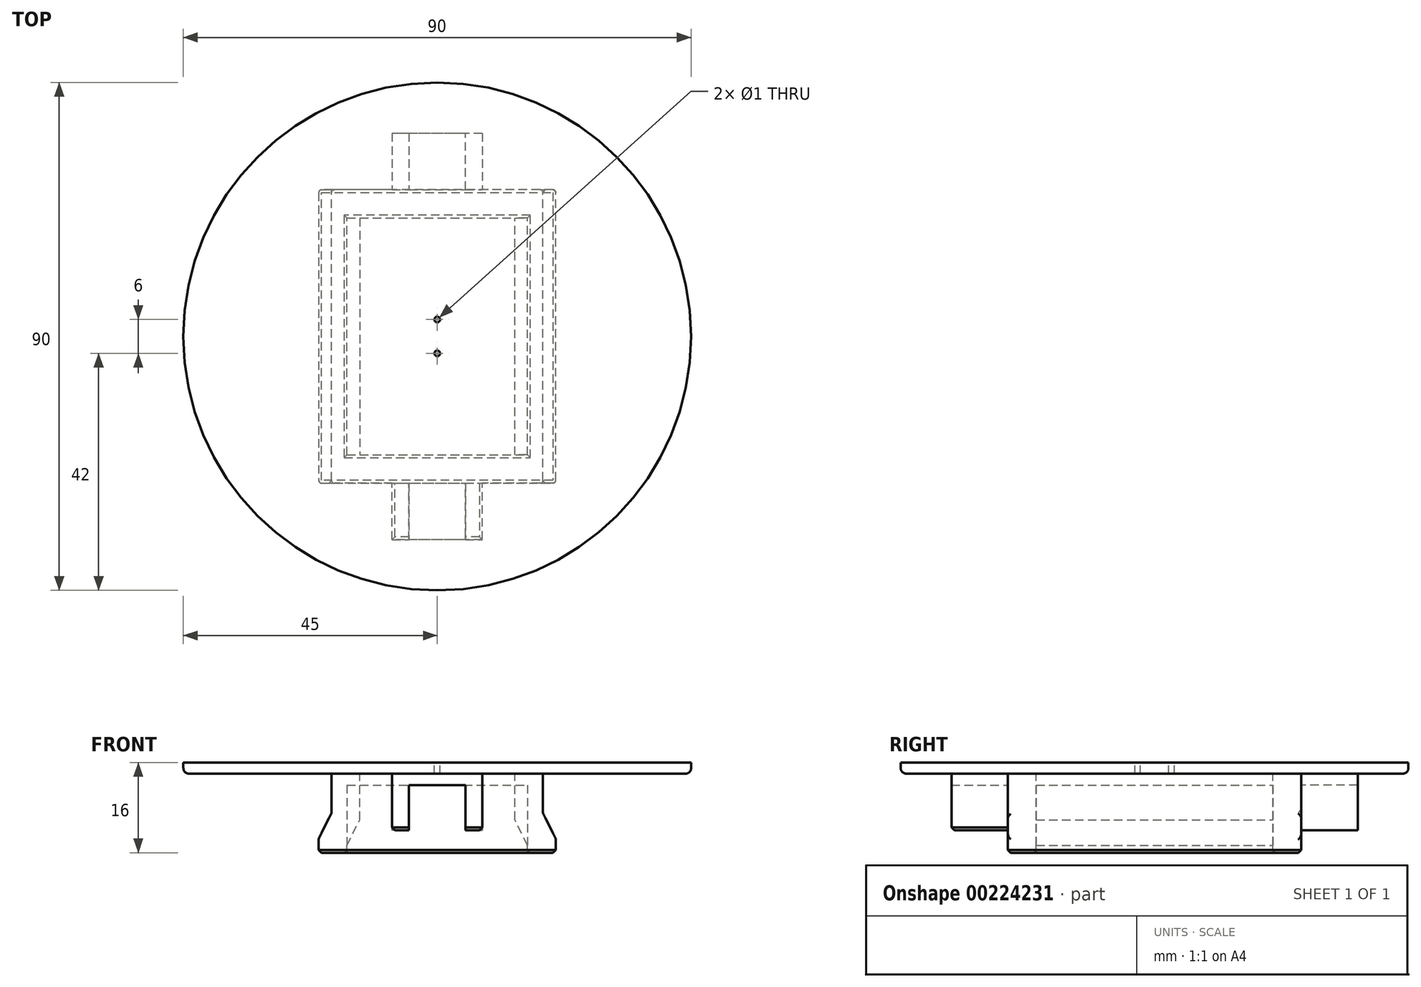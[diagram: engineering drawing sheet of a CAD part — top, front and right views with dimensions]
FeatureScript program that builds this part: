
annotation { "Feature Type Name" : "Feature", "Feature Type Description" : "" }
export const myFeature = defineFeature(function(context is Context, id is Id, definition is map)
    precondition{}
    {
        {
            var Q0;
            Q0=qCreatedBy(makeId("Top.planeOp"),FACE);
            var sketch = newSketch(context, id + "F0", { "sketchPlane" : qUnion([Q0])});
            skCircle(sketch, "E0", {"center": v(0, 0) * mm, "radius": 45 * mm});
            skSolve(sketch);
        }
        {
            var Q0;
            Q0 = qSketchRegion(id + "F0", true);
            extrude(context, id + "F1", {"entities" : qUnion([Q0]), "depth" : 2 * mm});
        }
        {
            var Q0;
            Q0=qCreatedBy(makeId("Front.planeOp"),FACE);
            var sketch = newSketch(context, id + "F2", { "sketchPlane" : qUnion([Q0])});
            skPoint(sketch, "E1.MirrorCS.end.orphan", {"position": v(0, -14) * mm});
            skPoint(sketch, "E2.MirrorCS.start.orphan", {"position": v(0, 0) * mm});
            skLineSegment(sketch, "E3", {"start": v(-18.75, -7) * mm, "end": v(-18.75, -14) * mm, "construction": true});
            skLineSegment(sketch, "E4", {"start": v(-18.75, -7) * mm, "end": v(-18.75, 0) * mm});
            skLineSegment(sketch, "E5", {"start": v(-21, -14) * mm, "end": v(-21, -11.5) * mm});
            skLineSegment(sketch, "E6", {"start": v(-21, -11.5) * mm, "end": v(-18.75, -7) * mm});
            skLineSegment(sketch, "E7", {"start": v(-18.75, 0) * mm, "end": v(0, 0) * mm});
            skLineSegment(sketch, "E8", {"start": v(-21, -14) * mm, "end": v(0, -14) * mm});
            skLineSegment(sketch, "E9", {"start": v(0, 0) * mm, "end": v(0, -14) * mm, "construction": true});
            skLineSegment(sketch, "E10.MirrorCS", {"start": v(21, -14) * mm, "end": v(21, -11.5) * mm});
            skLineSegment(sketch, "E11.MirrorCS", {"start": v(18.75, 0) * mm, "end": v(0, 0) * mm});
            skLineSegment(sketch, "E12.MirrorCS", {"start": v(21, -14) * mm, "end": v(0, -14) * mm});
            skLineSegment(sketch, "E13.MirrorCS", {"start": v(18.75, -7) * mm, "end": v(18.75, -14) * mm, "construction": true});
            skLineSegment(sketch, "E14.MirrorCS", {"start": v(18.75, -7) * mm, "end": v(18.75, 0) * mm});
            skLineSegment(sketch, "E15.MirrorCS", {"start": v(21, -11.5) * mm, "end": v(18.75, -7) * mm});
            skSolve(sketch);
        }
        {
            var Q0;
            Q0=makeQuery(id+"F2.imprint","IMPRINT",FACE,{"disambiguationData":[TD([[makeQuery(id+"F2.imprint","IMPRINT",EDGE,{"derivedFrom":sQuery(id+"F2.wireOp",EDGE,"E4")}),-1.0]])]});
            extrude(context, id + "F3", {"entities" : qUnion([Q0]), "operationType" : NewBodyOperationType.ADD, "depth" : 26 * mm, "hasSecondDirection" : true, "secondDirectionOppositeDirection" : true, "secondDirectionDepth" : 26 * mm});
        }
        {
            var Q0;
            Q0=makeQuery(id+"F3.opExtrude","SWEPT_FACE",FACE,{"disambiguationData":[OSD([sQuery(id+"F2.wireOp",EDGE,"E8"),sQuery(id+"F2.wireOp",EDGE,"E12.MirrorCS")])]});
            shell(context, id + "F4", {"entities" : qUnion([Q0]), "thickness" : 5 * mm});
        }
        {
            var Q0;
            Q0=makeQuery(id+"F1.opExtrude","CAP_FACE",FACE,{"disambiguationData":[OSD([sQuery(id+"F0.wireOp",EDGE,"E0")])],"isStart":false});
            var sketch = newSketch(context, id + "F5", { "sketchPlane" : qUnion([Q0])});
            skLineSegment(sketch, "E16", {"start": v(0, 3) * mm, "end": v(0, -3) * mm, "construction": true});
            skSolve(sketch);
        }
        {
            var Q0;
            Q0=sQuery(id+"F5.wireOp",VERTEX,"E16.end");
            var Q1;
            Q1=sQuery(id+"F5.wireOp",VERTEX,"E16.start");
            var Q2;
            Q2=makeQuery(id+"F1.opExtrude","SWEPT_BODY",BODY,{"disambiguationData":[OSD([sQuery(id+"F0.wireOp",EDGE,"E0")])]});
            hole(context, id + "F6", {"style" : HoleStyle.SIMPLE, "endStyle" : HoleEndStyle.THROUGH, "holeDiameter" : 1 * mm, "tappedDepth" : 12 * mm, "tapClearance" : 3, "locations" : qUnion([Q0, Q1]), "scope" : qUnion([Q2])});
        }
        {
            var Q0;
            Q0=makeQuery(id+"F1.opExtrude","CAP_EDGE",EDGE,{"disambiguationData":[OSD([sQuery(id+"F0.wireOp",EDGE,"E0")])],"isStart":true});
            fillet(context, id + "F7", {"entities" : qUnion([Q0]), "radius" : 1 * mm, "tangentPropagation" : true, "allowEdgeOverflow" : false});
        }
        {
            var Q0;
            Q0=makeQuery(id+"F3.opExtrude","SWEPT_EDGE",EDGE,{"disambiguationData":[OSD([sQuery(id+"F2.wireOp",EDGE,"E5"),sQuery(id+"F2.wireOp",EDGE,"E6")])]});
            var Q1;
            Q1=makeQuery(id+"F3.opExtrude","SWEPT_EDGE",EDGE,{"disambiguationData":[OSD([sQuery(id+"F2.wireOp",EDGE,"E4"),sQuery(id+"F2.wireOp",EDGE,"E6")])]});
            var Q2;
            Q2=makeQuery(id+"F3.opExtrude","CAP_EDGE",EDGE,{"disambiguationData":[OSD([sQuery(id+"F2.wireOp",EDGE,"E4")])],"isStart":false});
            var Q3;
            Q3=makeQuery(id+"F3.opExtrude","CAP_EDGE",EDGE,{"disambiguationData":[OSD([sQuery(id+"F2.wireOp",EDGE,"E5")])],"isStart":false});
            var Q4;
            Q4=makeQuery(id+"F3.opExtrude","CAP_EDGE",EDGE,{"disambiguationData":[OSD([sQuery(id+"F2.wireOp",EDGE,"E5")])],"isStart":true});
            var Q5;
            Q5=makeQuery(id+"F3.opExtrude","CAP_EDGE",EDGE,{"disambiguationData":[OSD([sQuery(id+"F2.wireOp",EDGE,"E6")])],"isStart":true});
            var Q6;
            Q6=makeQuery(id+"F3.opExtrude","SWEPT_EDGE",EDGE,{"disambiguationData":[OSD([sQuery(id+"F2.wireOp",EDGE,"E14.MirrorCS"),sQuery(id+"F2.wireOp",EDGE,"E15.MirrorCS")])]});
            var Q7;
            Q7=makeQuery(id+"F3.opExtrude","SWEPT_EDGE",EDGE,{"disambiguationData":[OSD([sQuery(id+"F2.wireOp",EDGE,"E10.MirrorCS"),sQuery(id+"F2.wireOp",EDGE,"E15.MirrorCS")])]});
            var Q8;
            Q8=makeQuery(id+"F3.opExtrude","CAP_EDGE",EDGE,{"disambiguationData":[OSD([sQuery(id+"F2.wireOp",EDGE,"E14.MirrorCS")])],"isStart":true});
            var Q9;
            Q9=makeQuery(id+"F3.opExtrude","CAP_EDGE",EDGE,{"disambiguationData":[OSD([sQuery(id+"F2.wireOp",EDGE,"E10.MirrorCS")])],"isStart":true});
            var Q10;
            Q10=makeQuery(id+"F3.opExtrude","CAP_EDGE",EDGE,{"disambiguationData":[OSD([sQuery(id+"F2.wireOp",EDGE,"E10.MirrorCS")])],"isStart":false});
            var Q11;
            Q11=makeQuery(id+"F3.opExtrude","CAP_EDGE",EDGE,{"disambiguationData":[OSD([sQuery(id+"F2.wireOp",EDGE,"E14.MirrorCS")])],"isStart":false});
            fillet(context, id + "F8", {"entities" : qUnion([Q0, Q1, Q2, Q3, Q4, Q5, Q6, Q7, Q8, Q9, Q10, Q11]), "radius" : .5 * mm, "tangentPropagation" : true, "allowEdgeOverflow" : false});
        }
        {
            var Q0;
            Q0=makeQuery(id+"F4.opShell","OFFSET_FACE",FACE,{"disambiguationData":[OSD([sQuery(id+"F0.wireOp",EDGE,"E0")])]});
            extrude(context, id + "F9", {"entities" : qUnion([Q0]), "operationType" : NewBodyOperationType.REMOVE, "oppositeDirection" : true, "depth" : 3 * mm});
        }
        {
            var Q0;
            Q0=makeQuery(id+"F3.opExtrude","CAP_FACE",FACE,{"disambiguationData":[OSD([sQuery(id+"F2.wireOp",EDGE,"E4"),sQuery(id+"F2.wireOp",EDGE,"E5"),sQuery(id+"F2.wireOp",EDGE,"E6"),sQuery(id+"F2.wireOp",EDGE,"E7"),sQuery(id+"F2.wireOp",EDGE,"E8"),sQuery(id+"F2.wireOp",EDGE,"E10.MirrorCS"),sQuery(id+"F2.wireOp",EDGE,"E11.MirrorCS"),sQuery(id+"F2.wireOp",EDGE,"E12.MirrorCS"),sQuery(id+"F2.wireOp",EDGE,"E14.MirrorCS"),sQuery(id+"F2.wireOp",EDGE,"E15.MirrorCS")])],"isStart":false});
            var sketch = newSketch(context, id + "F10", { "sketchPlane" : qUnion([Q0])});
            skLineSegment(sketch, "E17", {"start": v(0, 0) * mm, "end": v(8, 0) * mm});
            skLineSegment(sketch, "E18", {"start": v(8, 0) * mm, "end": v(8, -10) * mm});
            skLineSegment(sketch, "E19", {"start": v(8, -10) * mm, "end": v(-8, -10) * mm});
            skLineSegment(sketch, "E20", {"start": v(-8, -10) * mm, "end": v(-8, 0) * mm});
            skLineSegment(sketch, "E21", {"start": v(-8, 0) * mm, "end": v(0, 0) * mm});
            skSolve(sketch);
        }
        {
            var Q0;
            Q0 = qSketchRegion(id + "F10", true);
            extrude(context, id + "F11", {"entities" : qUnion([Q0]), "depth" : 10 * mm, "offsetDistance" : 25 * mm, "hasSecondDirection" : true, "secondDirectionOppositeDirection" : true, "secondDirectionDepth" : 2 * mm});
        }
        {
            var Q0;
            Q0=makeQuery(id+"F11.opExtrude","SWEPT_BODY",BODY,{"disambiguationData":[OSD([sQuery(id+"F10.wireOp",EDGE,"E17"),sQuery(id+"F10.wireOp",EDGE,"E18"),sQuery(id+"F10.wireOp",EDGE,"E19"),sQuery(id+"F10.wireOp",EDGE,"E20"),sQuery(id+"F10.wireOp",EDGE,"E21")])]});
            var Q1;
            Q1=qCreatedBy(makeId("Front.planeOp"),FACE);
            mirror(context, id + "F12", {"operationType" : NewBodyOperationType.ADD, "entities" : qUnion([Q0]), "mirrorPlane" : qUnion([Q1])});
        }
        {
            var Q0;
            {var subQ0=makeQuery(id+"F11.opExtrude","SWEPT_FACE",FACE,{"disambiguationData":[OSD([sQuery(id+"F10.wireOp",EDGE,"E19")])]});Q0=makeQuery(id+"F12.boolean.opBoolean","MERGE",FACE,{"derivedFrom":[makeQuery(id+"F3.opExtrude","SWEPT_FACE",FACE,{"disambiguationData":[OSD([sQuery(id+"F2.wireOp",EDGE,"E8"),sQuery(id+"F2.wireOp",EDGE,"E12.MirrorCS")])]}),subQ0,makeQuery(id+"F12.opPattern","COPY",FACE,{"derivedFrom":subQ0,"instanceName":"1"})]});}
            var sketch = newSketch(context, id + "F13", { "sketchPlane" : qUnion([Q0])});
            skLineSegment(sketch, "E22", {"start": v(0, -36) * mm, "end": v(-5, -36) * mm});
            skLineSegment(sketch, "E23", {"start": v(-5, -36) * mm, "end": v(-5, -21) * mm});
            skLineSegment(sketch, "E24", {"start": v(-5, -21) * mm, "end": v(5, -21) * mm});
            skLineSegment(sketch, "E25", {"start": v(5, -21) * mm, "end": v(5, -36) * mm});
            skLineSegment(sketch, "E26", {"start": v(5, -36) * mm, "end": v(0, -36) * mm});
            skSolve(sketch);
        }
        {
            var Q0;
            Q0=makeQuery(id+"F13.imprint","IMPRINT",FACE,{"disambiguationData":[TD([[makeQuery(id+"F13.imprint","IMPRINT",EDGE,{"derivedFrom":sQuery(id+"F13.wireOp",EDGE,"E22")}),-1.0]])]});
            var Q1;
            {var subQ0=sQuery(id+"F13.wireOp",EDGE,"E24");Q1=makeQuery(id+"F13.imprint","IMPRINT",FACE,{"disambiguationData":[TD([[makeQuery(id+"F13.imprint","IMPRINT",EDGE,{"derivedFrom":subQ0}),1.0]])]});}
            extrude(context, id + "F14", {"entities" : qUnion([Q0, Q1]), "oppositeDirection" : true, "depth" : 12 * mm, "offsetDistance" : 25 * mm});
        }
        {
            var Q0;
            Q0=makeQuery(id+"F14.opExtrude","SWEPT_BODY",BODY,{"disambiguationData":[OSD([sQuery(id+"F13.wireOp",EDGE,"E22"),sQuery(id+"F13.wireOp",EDGE,"E23"),sQuery(id+"F13.wireOp",EDGE,"E24"),sQuery(id+"F13.wireOp",EDGE,"E25"),sQuery(id+"F13.wireOp",EDGE,"E26")])]});
            var Q1;
            Q1=qCreatedBy(makeId("Front.planeOp"),FACE);
            mirror(context, id + "F15", {"entities" : qUnion([Q0]), "mirrorPlane" : qUnion([Q1])});
        }
        {
            var Q0;
            Q0=makeQuery(id+"F14.opExtrude","SWEPT_BODY",BODY,{"disambiguationData":[OSD([sQuery(id+"F13.wireOp",EDGE,"E22"),sQuery(id+"F13.wireOp",EDGE,"E23"),sQuery(id+"F13.wireOp",EDGE,"E24"),sQuery(id+"F13.wireOp",EDGE,"E25"),sQuery(id+"F13.wireOp",EDGE,"E26")])]});
            var Q1;
            Q1=makeQuery(id+"F15.opPattern","COPY",BODY,{"derivedFrom":makeQuery(id+"F14.opExtrude","SWEPT_BODY",BODY,{"disambiguationData":[OSD([sQuery(id+"F13.wireOp",EDGE,"E22"),sQuery(id+"F13.wireOp",EDGE,"E23"),sQuery(id+"F13.wireOp",EDGE,"E24"),sQuery(id+"F13.wireOp",EDGE,"E25"),sQuery(id+"F13.wireOp",EDGE,"E26")])]}),"instanceName":"1"});
            var Q2;
            Q2=makeQuery(id+"F1.opExtrude","SWEPT_BODY",BODY,{"disambiguationData":[OSD([sQuery(id+"F0.wireOp",EDGE,"E0")])]});
            booleanBodies(context, id + "F16", {"operationType" : BooleanOperationType.SUBTRACTION, "tools" : qUnion([Q0, Q1]), "targets" : qUnion([Q2])});
        }
        {
            var Q0;
            {var subQ0=sQuery(id+"F2.wireOp",EDGE,"E12.MirrorCS");var subQ1=sQuery(id+"F2.wireOp",EDGE,"E10.MirrorCS");var subQ2=sQuery(id+"F2.wireOp",EDGE,"E8");var subQ4=makeQuery(id+"F3.opExtrude","CAP_EDGE",EDGE,{"disambiguationData":[OSD([subQ2,subQ0])],"isStart":false});Q0=makeQuery(id+"FFm1TcCdVZ59tot_1.boolean.opBoolean","SPLIT",EDGE,{"disambiguationData":[TD([makeQuery(id+"F3.opExtrude","SWEPT_FACE",FACE,{"disambiguationData":[OSD([subQ1])]})])],"derivedFrom":subQ4});}
            var Q1;
            {var subQ0=sQuery(id+"F2.wireOp",EDGE,"E12.MirrorCS");var subQ1=sQuery(id+"F2.wireOp",EDGE,"E8");var subQ2=sQuery(id+"F2.wireOp",EDGE,"E5");Q1=makeQuery(id+"FFm1TcCdVZ59tot_1.boolean.opBoolean","SPLIT",EDGE,{"disambiguationData":[TD([makeQuery(id+"F3.opExtrude","SWEPT_FACE",FACE,{"disambiguationData":[OSD([subQ2])]})])],"derivedFrom":makeQuery(id+"F3.opExtrude","CAP_EDGE",EDGE,{"disambiguationData":[OSD([subQ1,subQ0])],"isStart":true})});}
            var Q2;
            {var subQ0=sQuery(id+"F2.wireOp",EDGE,"E12.MirrorCS");var subQ1=sQuery(id+"F2.wireOp",EDGE,"E8");var subQ8=sQuery(id+"F2.wireOp",EDGE,"E5");var subQ11=makeQuery(id+"F3.opExtrude","CAP_EDGE",EDGE,{"disambiguationData":[OSD([subQ1,subQ0])],"isStart":false});Q2=makeQuery(id+"FFm1TcCdVZ59tot_1.boolean.opBoolean","SPLIT",EDGE,{"disambiguationData":[TD([makeQuery(id+"F4.opShell","OFFSET_FACE",FACE,{"disambiguationData":[OSD([subQ8])]})])],"derivedFrom":makeQuery(id+"F4.opShell","OFFSET_EDGE",EDGE,{"disambiguationData":[OSD([subQ1,subQ0]),TDD([subQ11])]})});}
            var Q3;
            {var subQ0=sQuery(id+"F2.wireOp",EDGE,"E12.MirrorCS");var subQ1=sQuery(id+"F2.wireOp",EDGE,"E8");var subQ5=sQuery(id+"F2.wireOp",EDGE,"E10.MirrorCS");Q3=makeQuery(id+"FFm1TcCdVZ59tot_1.boolean.opBoolean","SPLIT",EDGE,{"disambiguationData":[TD([makeQuery(id+"F4.opShell","OFFSET_FACE",FACE,{"disambiguationData":[OSD([subQ5])]})])],"derivedFrom":makeQuery(id+"F4.opShell","OFFSET_EDGE",EDGE,{"disambiguationData":[OSD([subQ1,subQ0]),TDD([makeQuery(id+"F3.opExtrude","CAP_EDGE",EDGE,{"disambiguationData":[OSD([subQ1,subQ0])],"isStart":true})])]})});}
            var Q4;
            Q4=makeQuery(id+"F4.opShell","OFFSET_EDGE",EDGE,{"disambiguationData":[OSD([sQuery(id+"F2.wireOp",EDGE,"E10.MirrorCS"),sQuery(id+"F2.wireOp",EDGE,"E12.MirrorCS")])]});
            var Q5;
            {var subQ0=sQuery(id+"F2.wireOp",EDGE,"E12.MirrorCS");var subQ1=sQuery(id+"F2.wireOp",EDGE,"E8");var subQ5=sQuery(id+"F2.wireOp",EDGE,"E10.MirrorCS");var subQ11=makeQuery(id+"F3.opExtrude","CAP_EDGE",EDGE,{"disambiguationData":[OSD([subQ1,subQ0])],"isStart":false});Q5=makeQuery(id+"FFm1TcCdVZ59tot_1.boolean.opBoolean","SPLIT",EDGE,{"disambiguationData":[TD([makeQuery(id+"F4.opShell","OFFSET_FACE",FACE,{"disambiguationData":[OSD([subQ5])]})])],"derivedFrom":makeQuery(id+"F4.opShell","OFFSET_EDGE",EDGE,{"disambiguationData":[OSD([subQ1,subQ0]),TDD([subQ11])]})});}
            var Q6;
            Q6=makeQuery(id+"F4.opShell","OFFSET_EDGE",EDGE,{"disambiguationData":[OSD([sQuery(id+"F2.wireOp",EDGE,"E5"),sQuery(id+"F2.wireOp",EDGE,"E8")])]});
            var Q7;
            {var subQ0=sQuery(id+"F2.wireOp",EDGE,"E12.MirrorCS");var subQ1=sQuery(id+"F2.wireOp",EDGE,"E8");var subQ8=sQuery(id+"F2.wireOp",EDGE,"E5");Q7=makeQuery(id+"FFm1TcCdVZ59tot_1.boolean.opBoolean","SPLIT",EDGE,{"disambiguationData":[TD([makeQuery(id+"F4.opShell","OFFSET_FACE",FACE,{"disambiguationData":[OSD([subQ8])]})])],"derivedFrom":makeQuery(id+"F4.opShell","OFFSET_EDGE",EDGE,{"disambiguationData":[OSD([subQ1,subQ0]),TDD([makeQuery(id+"F3.opExtrude","CAP_EDGE",EDGE,{"disambiguationData":[OSD([subQ1,subQ0])],"isStart":true})])]})});}
            var Q8;
            Q8=makeQuery(id+"F11.opExtrude","SWEPT_EDGE",EDGE,{"disambiguationData":[OSD([sQuery(id+"F2.wireOp",EDGE,"E8"),sQuery(id+"F2.wireOp",EDGE,"E12.MirrorCS"),sQuery(id+"F10.wireOp",EDGE,"E18"),sQuery(id+"F10.wireOp",EDGE,"E19")])]});
            var Q9;
            Q9=makeQuery(id+"F11.opExtrude","CAP_EDGE",EDGE,{"disambiguationData":[OSD([sQuery(id+"F10.wireOp",EDGE,"E19")])],"isStart":false});
            var Q10;
            Q10=makeQuery(id+"F11.opExtrude","SWEPT_EDGE",EDGE,{"disambiguationData":[OSD([sQuery(id+"F2.wireOp",EDGE,"E8"),sQuery(id+"F2.wireOp",EDGE,"E12.MirrorCS"),sQuery(id+"F10.wireOp",EDGE,"E19"),sQuery(id+"F10.wireOp",EDGE,"E20")])]});
            chamfer(context, id + "F17", {"entities" : qUnion([Q0, Q1, Q2, Q3, Q4, Q5, Q6, Q7, Q8, Q9, Q10]), "width" : .5 * mm, "tangentPropagation" : true});
        }
    });
